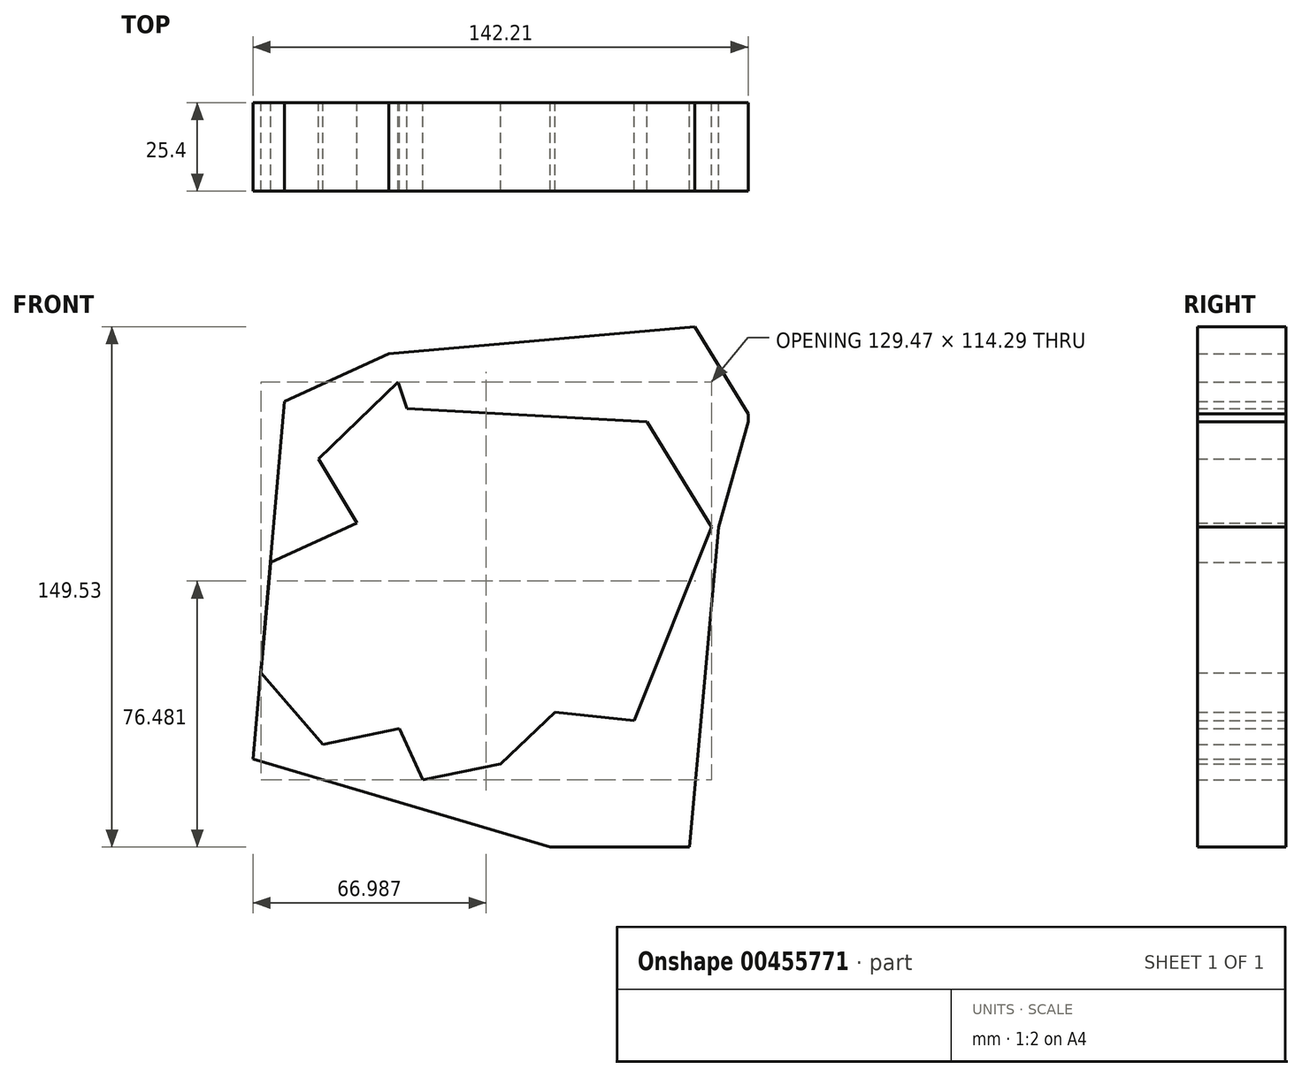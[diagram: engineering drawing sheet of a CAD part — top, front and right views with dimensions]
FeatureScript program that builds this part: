
annotation { "Feature Type Name" : "Feature", "Feature Type Description" : "" }
export const myFeature = defineFeature(function(context is Context, id is Id, definition is map)
    precondition{}
    {
        {
            var Q0;
            Q0=qCreatedBy(makeId("Front.planeOp"),FACE);
            var sketch = newSketch(context, id + "F0", { "sketchPlane" : qUnion([Q0])});
            skLineSegment(sketch, "E0", {"start": v(-31.71, 67.33) * mm, "end": v(14.64, -74.4) * mm});
            skLineSegment(sketch, "E1", {"start": v(14.64, -74.4) * mm, "end": v(-61.72, 53.67) * mm});
            skLineSegment(sketch, "E2", {"start": v(-61.72, 53.67) * mm, "end": v(42.44, 47.81) * mm});
            skLineSegment(sketch, "E3", {"start": v(42.44, 47.81) * mm, "end": v(-70.74, -49.03) * mm});
            skLineSegment(sketch, "E4", {"start": v(-70.74, -49.03) * mm, "end": v(1.47, -34.15) * mm});
            skLineSegment(sketch, "E5", {"start": v(1.47, -34.15) * mm, "end": v(42.44, 47.81) * mm});
            skLineSegment(sketch, "E6", {"start": v(60.98, 17.56) * mm, "end": v(42.44, 47.81) * mm});
            skLineSegment(sketch, "E7", {"start": v(60.98, 17.56) * mm, "end": v(1.47, -34.15) * mm});
            skLineSegment(sketch, "E8", {"start": v(1.47, -34.15) * mm, "end": v(38.79, -38.06) * mm});
            skLineSegment(sketch, "E9", {"start": v(38.79, -38.06) * mm, "end": v(14.64, -74.4) * mm});
            skLineSegment(sketch, "E10", {"start": v(38.79, -38.06) * mm, "end": v(60.98, 17.56) * mm});
            skLineSegment(sketch, "E11", {"start": v(62.93, 17.56) * mm, "end": v(71.47, 47.81) * mm});
            skLineSegment(sketch, "E12", {"start": v(71.47, 47.81) * mm, "end": v(42.44, 47.81) * mm});
            skLineSegment(sketch, "E13", {"start": v(62.93, 17.56) * mm, "end": v(60.98, 17.56) * mm});
            skLineSegment(sketch, "E14", {"start": v(42.44, 47.81) * mm, "end": v(56.1, 75.13) * mm});
            skLineSegment(sketch, "E15", {"start": v(56.1, 75.13) * mm, "end": v(71.47, 50.06) * mm});
            skLineSegment(sketch, "E16", {"start": v(71.47, 50.06) * mm, "end": v(71.47, 47.81) * mm});
            skLineSegment(sketch, "E17", {"start": v(56.1, 75.13) * mm, "end": v(-31.71, 67.33) * mm});
            skLineSegment(sketch, "E18", {"start": v(-61.72, 53.67) * mm, "end": v(-31.71, 67.33) * mm});
            skLineSegment(sketch, "E19", {"start": v(-61.72, 50.06) * mm, "end": v(-70.74, -49.03) * mm});
            skLineSegment(sketch, "E20", {"start": v(-61.72, 53.67) * mm, "end": v(-70.74, -49.03) * mm});
            skLineSegment(sketch, "E21", {"start": v(-70.74, -49.03) * mm, "end": v(14.64, -74.4) * mm});
            skLineSegment(sketch, "E22", {"start": v(62.93, 17.56) * mm, "end": v(54.56, -74.4) * mm});
            skLineSegment(sketch, "E23", {"start": v(54.56, -74.4) * mm, "end": v(14.64, -74.4) * mm});
            skLineSegment(sketch, "E24", {"start": v(4.85, 70.58) * mm, "end": v(4.85, 15.65) * mm});
            skLineSegment(sketch, "E25", {"start": v(4.85, 15.65) * mm, "end": v(18.5, -0.07) * mm});
            skLineSegment(sketch, "E26", {"start": v(18.5, -0.07) * mm, "end": v(29.32, -9.95) * mm});
            skLineSegment(sketch, "E27", {"start": v(29.32, -9.95) * mm, "end": v(38.79, -38.06) * mm});
            skLineSegment(sketch, "E28", {"start": v(38.79, -38.06) * mm, "end": v(54.56, -74.4) * mm});
            skLineSegment(sketch, "E29", {"start": v(-28.05, -42.2) * mm, "end": v(-28.66, -40.36) * mm});
            skLineSegment(sketch, "E30", {"start": v(-28.66, -40.36) * mm, "end": v(-17.43, -64.87) * mm});
            skLineSegment(sketch, "E31", {"start": v(-17.43, -64.87) * mm, "end": v(-37.65, -20.72) * mm});
            skLineSegment(sketch, "E32", {"start": v(-37.65, -20.72) * mm, "end": v(-65.6, 7.4) * mm});
            skLineSegment(sketch, "E33", {"start": v(-65.6, 7.4) * mm, "end": v(-40.88, 18.72) * mm});
            skLineSegment(sketch, "E34", {"start": v(-40.88, 18.72) * mm, "end": v(-20, 31.52) * mm});
            skLineSegment(sketch, "E35", {"start": v(-20, 31.52) * mm, "end": v(4.85, 49.92) * mm});
            skLineSegment(sketch, "E36", {"start": v(4.85, 49.92) * mm, "end": v(31.33, 72.93) * mm});
            skLineSegment(sketch, "E37", {"start": v(31.33, 72.93) * mm, "end": v(42.44, 47.81) * mm});
            skLineSegment(sketch, "E38", {"start": v(-19.57, 68.4) * mm, "end": v(-51.88, 37.17) * mm});
            skLineSegment(sketch, "E39", {"start": v(-51.88, 37.17) * mm, "end": v(-13.51, 11.67) * mm});
            skLineSegment(sketch, "E40", {"start": v(-13.51, 11.67) * mm, "end": v(-68.49, -24.32) * mm});
            skLineSegment(sketch, "E41", {"start": v(-68.49, -24.32) * mm, "end": v(-38.76, -58.53) * mm});
            skLineSegment(sketch, "E42", {"start": v(-38.76, -58.53) * mm, "end": v(0.37, -50.47) * mm});
            skLineSegment(sketch, "E43", {"start": v(0.37, -50.47) * mm, "end": v(32.66, -19.86) * mm});
            skLineSegment(sketch, "E44", {"start": v(32.66, -19.86) * mm, "end": v(33.52, 29.95) * mm});
            skLineSegment(sketch, "E45", {"start": v(33.52, 29.95) * mm, "end": v(69.89, 42.2) * mm});
            skLineSegment(sketch, "E46", {"start": v(69.89, 42.2) * mm, "end": v(4.85, 39.76) * mm});
            skLineSegment(sketch, "E47", {"start": v(4.85, 39.76) * mm, "end": v(-13.51, 11.67) * mm});
            skSolve(sketch);
        }
        {
            var Q0;
            Q0 = qSketchRegion(id + "F0", true);
            extrude(context, id + "F1", {"entities" : qUnion([Q0]), "depth" : 25.4 * mm});
        }
    });
